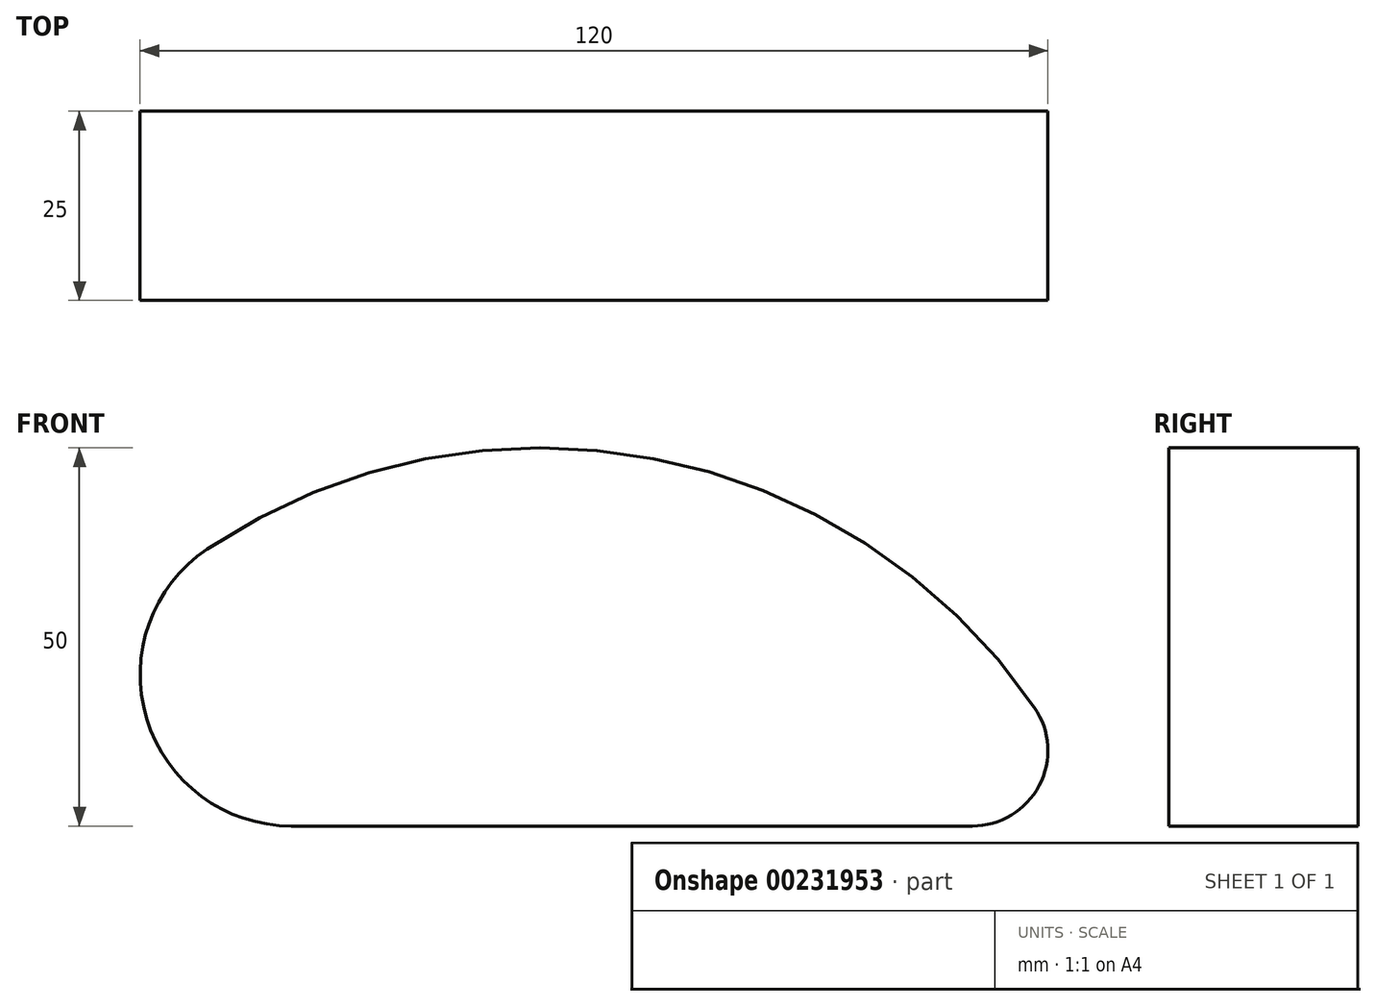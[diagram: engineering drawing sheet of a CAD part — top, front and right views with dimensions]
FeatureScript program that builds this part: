
annotation { "Feature Type Name" : "Feature", "Feature Type Description" : "" }
export const myFeature = defineFeature(function(context is Context, id is Id, definition is map)
    precondition{}
    {
        {
            var Q0;
            Q0=qCreatedBy(makeId("Front.planeOp"),FACE);
            var sketch = newSketch(context, id + "F0", { "sketchPlane" : qUnion([Q0])});
            skLineSegment(sketch, "E0", {"start": v(-30.21, -3.17) * mm, "end": v(59.79, -3.17) * mm});
            skArc(sketch, "E1", {"start": v(-30.21, -3.17) * mm, "mid": v(-49.35, 11.02) * mm, "end": v(-41.33, 33.45) * mm});
            skArc(sketch, "E2", {"start": v(-41.33, 33.45) * mm, "mid": v(17.65, 45.41) * mm, "end": v(68.03, 12.5) * mm});
            skArc(sketch, "E3", {"start": v(68.03, 12.5) * mm, "mid": v(68.64, 2.18) * mm, "end": v(59.79, -3.17) * mm});
            skSolve(sketch);
        }
        {
            var Q0;
            Q0=makeQuery(id+"F0.imprint","IMPRINT",FACE,{"disambiguationData":[TD([[makeQuery(id+"F0.imprint","IMPRINT",EDGE,{"derivedFrom":sQuery(id+"F0.wireOp",EDGE,"E0")}),1.0]])]});
            extrude(context, id + "F1", {"entities" : qUnion([Q0]), "depth" : 25 * mm});
        }
    });
